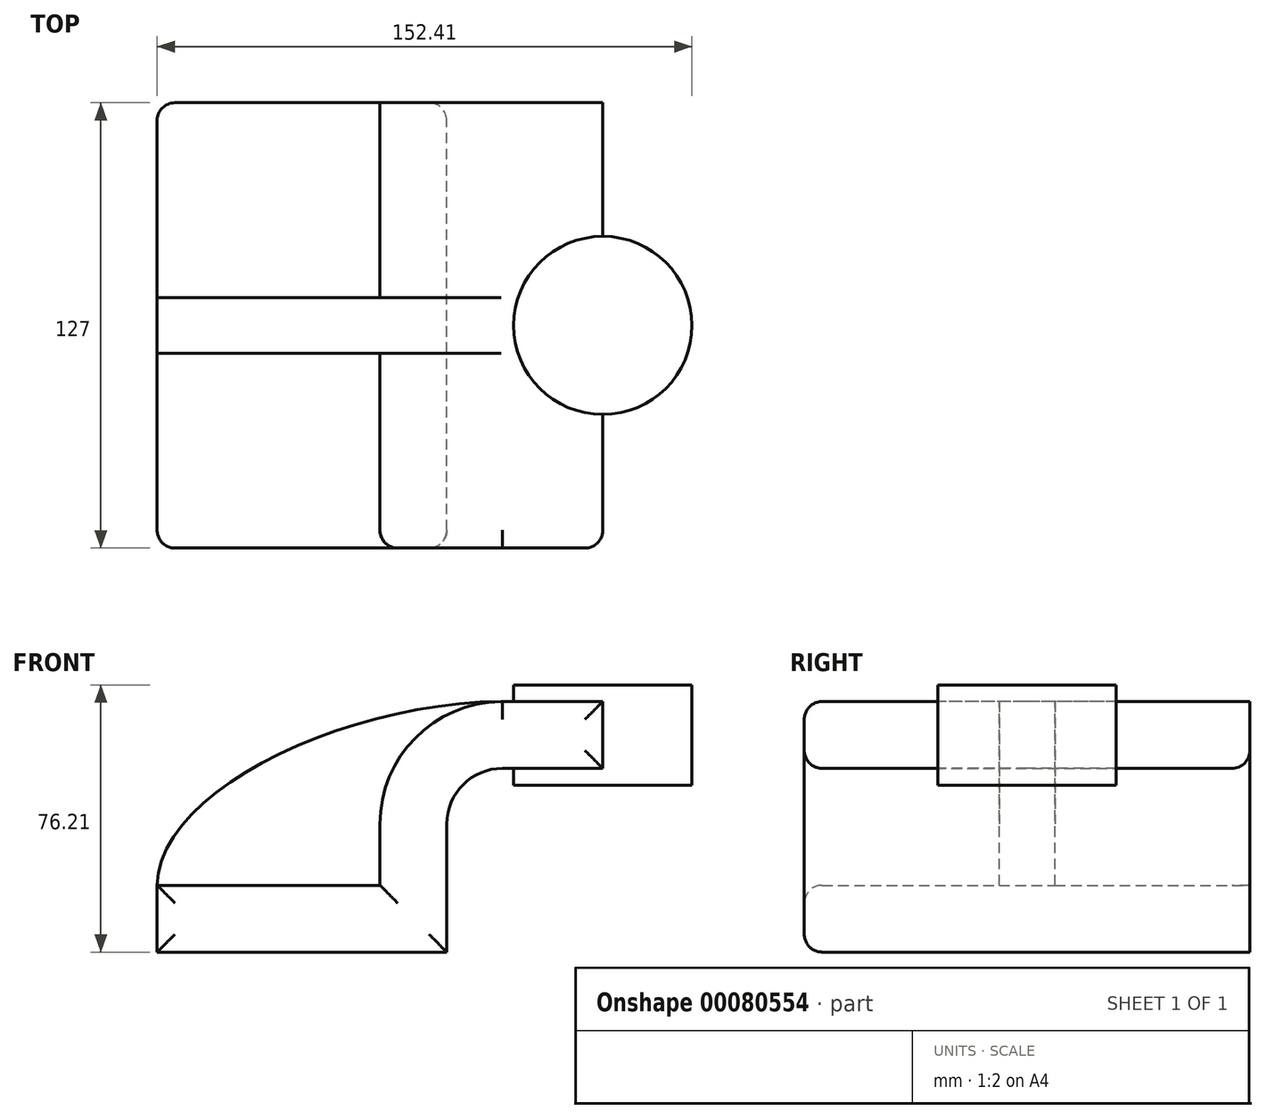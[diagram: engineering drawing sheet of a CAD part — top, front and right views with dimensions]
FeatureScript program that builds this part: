
annotation { "Feature Type Name" : "Feature", "Feature Type Description" : "" }
export const myFeature = defineFeature(function(context is Context, id is Id, definition is map)
    precondition{}
    {
        {
            var Q0;
            Q0=qCreatedBy(makeId("Front.planeOp"),FACE);
            var sketch = newSketch(context, id + "F0", { "sketchPlane" : qUnion([Q0])});
            skLineSegment(sketch, "E0.bottom", {"start": v(-41.28, -9.53) * mm, "end": v(41.28, -9.53) * mm});
            skLineSegment(sketch, "E0.top", {"start": v(-41.28, 9.53) * mm, "end": v(41.28, 9.53) * mm});
            skLineSegment(sketch, "E0.left", {"start": v(-41.28, -9.53) * mm, "end": v(-41.28, 9.53) * mm});
            skLineSegment(sketch, "E0.right", {"start": v(41.28, -9.53) * mm, "end": v(41.28, 9.53) * mm});
            skPoint(sketch, "E0.middle", {"position": v(0, 0) * mm});
            skLineSegment(sketch, "E1.bottom", {"start": v(60.32, 38.1) * mm, "end": v(111.12, 38.1) * mm});
            skLineSegment(sketch, "E1.top", {"start": v(60.32, 66.67) * mm, "end": v(111.12, 66.67) * mm});
            skLineSegment(sketch, "E1.left", {"start": v(60.32, 38.1) * mm, "end": v(60.32, 66.68) * mm});
            skLineSegment(sketch, "E1.right", {"start": v(111.12, 38.1) * mm, "end": v(111.12, 66.68) * mm});
            skPoint(sketch, "E1.middle", {"position": v(85.72, 52.39) * mm});
            skLineSegment(sketch, "E2", {"start": v(41.27, 9.53) * mm, "end": v(41.27, 27) * mm});
            skArc(sketch, "E3", {"start": v(41.27, 27) * mm, "mid": v(45.92, 38.23) * mm, "end": v(57.15, 42.88) * mm});
            skLineSegment(sketch, "E4", {"start": v(57.15, 42.88) * mm, "end": v(85.72, 42.88) * mm});
            skLineSegment(sketch, "E5.0", {"start": v(57.15, 61.93) * mm, "end": v(85.72, 61.93) * mm});
            skArc(sketch, "E5.1", {"start": v(22.23, 27) * mm, "mid": v(32.45, 51.7) * mm, "end": v(57.15, 61.93) * mm});
            skLineSegment(sketch, "E5.2", {"start": v(22.22, 9.53) * mm, "end": v(22.22, 27) * mm});
            skLineSegment(sketch, "E6", {"start": v(85.72, 38.1) * mm, "end": v(85.72, 66.67) * mm});
            skFitSpline(sketch, "E7", {"points": [v(-41.28, 9.53) * mm, v(57.15, 61.93) * mm], "startDerivative": vector(1.14, 81.2) * mm, "endDerivative": vector(135.05, 0.64) * mm});
            skSolve(sketch);
        }
        {
            var Q0;
            Q0=makeQuery(id+"F0.imprint","IMPRINT",FACE,{"disambiguationData":[TD([[makeQuery(id+"F0.imprint","IMPRINT",EDGE,{"derivedFrom":sQuery(id+"F0.wireOp",EDGE,"E0.bottom")}),1.0]])]});
            extrude(context, id + "F1", {"entities" : qUnion([Q0]), "endBound" : BoundingType.SYMMETRIC, "depth" : 127 * mm});
        }
        {
            var Q0;
            {var subQ1=sQuery(id+"F0.wireOp",EDGE,"E2");Q0=makeQuery(id+"F0.imprint","IMPRINT",FACE,{"disambiguationData":[TD([[makeQuery(id+"F0.imprint","IMPRINT",EDGE,{"derivedFrom":subQ1}),1.0]])]});}
            var Q1;
            {var subQ0=sQuery(id+"F0.wireOp",EDGE,"E4");var subQ1=sQuery(id+"F0.wireOp",EDGE,"E1.left");var subQ2=makeQuery(id+"F0.imprint","INTERSECT",VERTEX,{"derivedFrom":[subQ1,subQ0]});Q1=makeQuery(id+"F0.imprint","IMPRINT",FACE,{"disambiguationData":[TD([[makeQuery(id+"F0.imprint","IMPRINT",EDGE,{"disambiguationData":[TD([[subQ2,-1.0]])],"derivedFrom":subQ1}),-1.0]])]});}
            extrude(context, id + "F2", {"entities" : qUnion([Q0, Q1]), "operationType" : NewBodyOperationType.ADD, "endBound" : BoundingType.SYMMETRIC, "depth" : 127 * mm});
        }
        {
            var Q0;
            {var subQ3=sQuery(id+"F0.wireOp",EDGE,"E5.2");Q0=makeQuery(id+"F0.imprint","IMPRINT",FACE,{"disambiguationData":[TD([[makeQuery(id+"F0.imprint","IMPRINT",EDGE,{"derivedFrom":subQ3}),1.0]])]});}
            extrude(context, id + "F3", {"entities" : qUnion([Q0]), "operationType" : NewBodyOperationType.ADD, "endBound" : BoundingType.SYMMETRIC, "depth" : 15.88 * mm});
        }
        {
            var Q0;
            {var subQ0=sQuery(id+"F0.wireOp",EDGE,"E1.right");Q0=makeQuery(id+"F0.imprint","IMPRINT",FACE,{"disambiguationData":[TD([[makeQuery(id+"F0.imprint","IMPRINT",EDGE,{"derivedFrom":subQ0}),1.0]])]});}
            var Q1;
            Q1=sQuery(id+"F0.wireOp",EDGE,"E6");
            revolve(context, id + "F4", {"operationType" : NewBodyOperationType.ADD, "entities" : qUnion([Q0]), "axis" : qUnion([Q1]), "revolveType" : RevolveType.FULL});
        }
        {
            var Q0;
            {var subQ0=sQuery(id+"F0.wireOp",EDGE,"E0.top");Q0=makeQuery(id+"F2.boolean.opBoolean","MERGE",FACE,{"derivedFrom":[makeQuery(id+"F1.opExtrude","CAP_FACE",FACE,{"disambiguationData":[OSD([sQuery(id+"F0.wireOp",EDGE,"E0.bottom"),subQ0,sQuery(id+"F0.wireOp",EDGE,"E0.left"),sQuery(id+"F0.wireOp",EDGE,"E0.right")])],"isStart":false}),makeQuery(id+"F2.opExtrude","CAP_FACE",FACE,{"disambiguationData":[OSD([subQ0,sQuery(id+"F0.wireOp",EDGE,"E2"),sQuery(id+"F0.wireOp",EDGE,"E3"),sQuery(id+"F0.wireOp",EDGE,"E4"),sQuery(id+"F0.wireOp",EDGE,"E5.0"),sQuery(id+"F0.wireOp",EDGE,"E5.1"),sQuery(id+"F0.wireOp",EDGE,"E5.2"),sQuery(id+"F0.wireOp",EDGE,"E6"),sQuery(id+"F0.wireOp",EDGE,"E7")])],"isStart":false})]});}
            var Q1;
            Q1=makeQuery(id+"F2.boolean.opBoolean","MERGE",EDGE,{"derivedFrom":[makeQuery(id+"F1.opExtrude","CAP_EDGE",EDGE,{"disambiguationData":[OSD([sQuery(id+"F0.wireOp",EDGE,"E0.right")])],"isStart":false}),makeQuery(id+"F2.opExtrude","CAP_EDGE",EDGE,{"disambiguationData":[OSD([sQuery(id+"F0.wireOp",EDGE,"E2")])],"isStart":false})]});
            var Q2;
            Q2=makeQuery(id+"F2.boolean.opBoolean","MERGE",EDGE,{"derivedFrom":[makeQuery(id+"F1.opExtrude","CAP_EDGE",EDGE,{"disambiguationData":[OSD([sQuery(id+"F0.wireOp",EDGE,"E0.right")])],"isStart":true}),makeQuery(id+"F2.opExtrude","CAP_EDGE",EDGE,{"disambiguationData":[OSD([sQuery(id+"F0.wireOp",EDGE,"E2")])],"isStart":true})]});
            var Q3;
            Q3=makeQuery(id+"F1.opExtrude","CAP_EDGE",EDGE,{"disambiguationData":[OSD([sQuery(id+"F0.wireOp",EDGE,"E0.left")])],"isStart":true});
            var Q4;
            Q4=makeQuery(id+"F1.opExtrude","CAP_EDGE",EDGE,{"disambiguationData":[OSD([sQuery(id+"F0.wireOp",EDGE,"E0.left")])],"isStart":false});
            fillet(context, id + "F5", {"entities" : qUnion([Q0, Q1, Q2, Q3, Q4]), "radius" : 5.08 * mm, "tangentPropagation" : true, "allowEdgeOverflow" : false});
        }
    });
